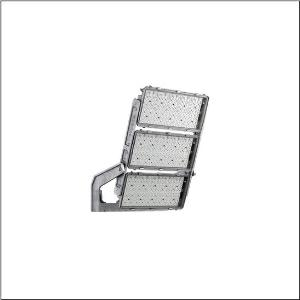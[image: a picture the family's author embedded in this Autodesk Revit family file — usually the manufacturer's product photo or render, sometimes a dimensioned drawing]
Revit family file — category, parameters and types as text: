
# Revit family: floodlight_fl_11_maxi_pro_remote___pl43_5xa779426a01aa_52e7
name_source: partatom
category: Lighting Fixtures
units: mm (PartAtom-declared; Revit-internal decimal feet)

## family parameters
Cut with Voids When Loaded = No
Host = Face
Light Source = No
Part Type = Normal
Room Calculation Point = No
Round Connector Dimension = Use Diameter
Shared = No

## types (1)
- --- (1 x LED, 172790 lm, 1387.6 W, 4000K)
    Apparent Load = 1388 VA
    CIE Flux Codes = 25 74 99 100 100
    Color Rendering = 70
    Color Temperature = 4000K
    Default Elevation = 1800 mm
    Description = Floodlight FL 11  maxi  pro Remote floodlight; light control with lens of PMMA; cover panel of toughened safety glass, transparent; light distribution: PL43, asymmetric direct distribution, LEDcolour temperature: 4000K, rated luminous flux: 172.790lm, colour rendering: CRI > 70, light colour: 740; luminous efficacy: 125lm/W; brightness control: DALI 2 (1 DALI address); with terminal, 8-pole, max. 2.5mm², mains connection: 220..240V/380..400V AC, 50/60Hz, surge voltage resistance: line to ground: 10kV, ECG replaceable separately, LED unit replaceable without ESD environment, dustproof LED module, dimming range 10..100%, no afterglow with DALI off / DMX off command; 1388W floodlight with 2x LED unit of diecast aluminium, coated grey; length: 713mm / width: 651mm / height: 338mm; mounting bracket, of diecast aluminium, uncoated, natural, equipment: Power, protection rating (complete): IP66; insulation class (complete): insulation class I (protective earthing); certification: CE, ENEC, VDE; ball protection: ball impact resistance with accessories, impact resistance: IK07; rated ambient temperature 10°C, only for outdoor installations, permissible operating ambient temperature: -40..+30°C, permissible storage temperature: -40..+85°C; packaging unit: 1 piece

Light Distribution: PL43
    Height = 320 mm
    Lamp = 1 x LED
    Lamp Light Flux = 172790 lm
    Lamp Power = 1387.6 W
    Lamp count = 1
    Length = 1002 mm
    Luminous efficacy = 125 lm/W
    Manufacturer = Siteco
    ModVariant = No
    Model = 5XA779426A01AA
    Mounting Place = Ceiling
    Mounting Type = Surface mounted
    Number of Poles = 1
    OnlyDefault = Yes
    Power Factor = 1
    Product Name = Floodlight FL 11 maxi pro Remote | PL43
    Product group = floodlight | ceiling mounted
    ProductGroupID = 302
    Protection Class = Protection class I
    Protection Degree = IP 66
    RLX_Detail_Level = 1
    RLX_Emergency_Light_Flux = 0 lm
    RLX_Emergency_Type = 0
    RLX_Emergency_Type_DB = No
    RlxData = <blob elided: 52449 chars, md5=fc856881>
    Socket = socket
    Standby Power = 0 W
    System Light Flux = 172790 lm
    System Power = 1388 W
    Type Comments = factory setting: luminous flux: 100 % | dim-lin: 254 | 955 mA
    Type Image = l_1006784.jpg
    URL = http://relux.com
    VarID = @adj_026847
    Voltage = 0 V
    Weight = 0.00 kg
    Width = 655 mm

## geometry (parser evidence)
native form markers: Blend x4, Sweep x13
no freeform markers — native parametric forms only
